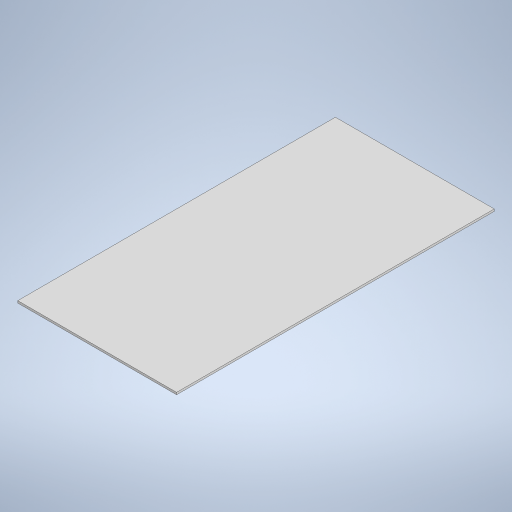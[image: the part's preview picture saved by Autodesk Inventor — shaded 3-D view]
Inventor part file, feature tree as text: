
AUTODESK INVENTOR PART (.ipt)
format: ipt  version: 2023 (Build 270158000, 158)  size: 209,920 bytes
history: native  units: mm
features: other x1, extrude x1, sketch x1
ambient origin geometry x8: Origin, YZ Plane, XZ Plane, XY Plane, X Axis, Y Axis, Z Axis, Center Point
bodies: Body1 (feature_tree)
feature tree (3):
  other  "Твердое тело1"
  extrude  "Выдавливание1"  Depth=300.0mm
  sketch  "Эскиз1"
